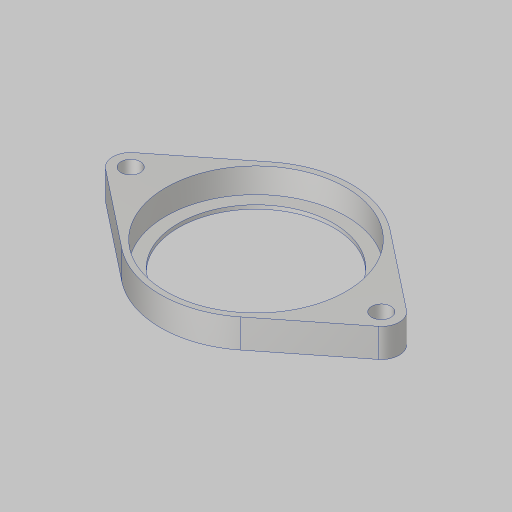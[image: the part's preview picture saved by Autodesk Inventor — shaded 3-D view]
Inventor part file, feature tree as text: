
AUTODESK INVENTOR PART (.ipt)
format: ipt  version: 2023.5 (Build 275446000, 446)  size: 129,024 bytes
history: native  units: in
note: dims shown in document units (in); Inventor stores cm internally (conversion verified against a paired STEP export)
features: sketch x2, extrude x2, hole x1
ambient origin geometry x8: Origin, YZ Plane, XZ Plane, XY Plane, X Axis, Y Axis, Z Axis, Center Point
bodies: Solid1 (feature_tree)
feature tree (5):
  sketch  "Sketch1"  dims[d0=1.875in d1=1.312in]
  extrude  "Extrusion1"  Depth=1.312in
  extrude  "Extrusion2"  Depth=1.0in
  hole  "Hole1"  [1 undecoded]
  sketch  "Sketch2"  dims[d2=0.375in d3=0.125in d4=0.0625in d5=0.3in d6=0.0in d7=1.885in d8=0.26in d9=0.0in d10=0.201in d11=0.75in d12=0.385in d13=0.25in d14=0.5635in d15=1.0in d16=0.8108in]
note: 1 required parameter value undecoded (feature->parameter linkage not recoverable at this tier; creation-order binding heuristic only, values carry confidence <= 0.55)
